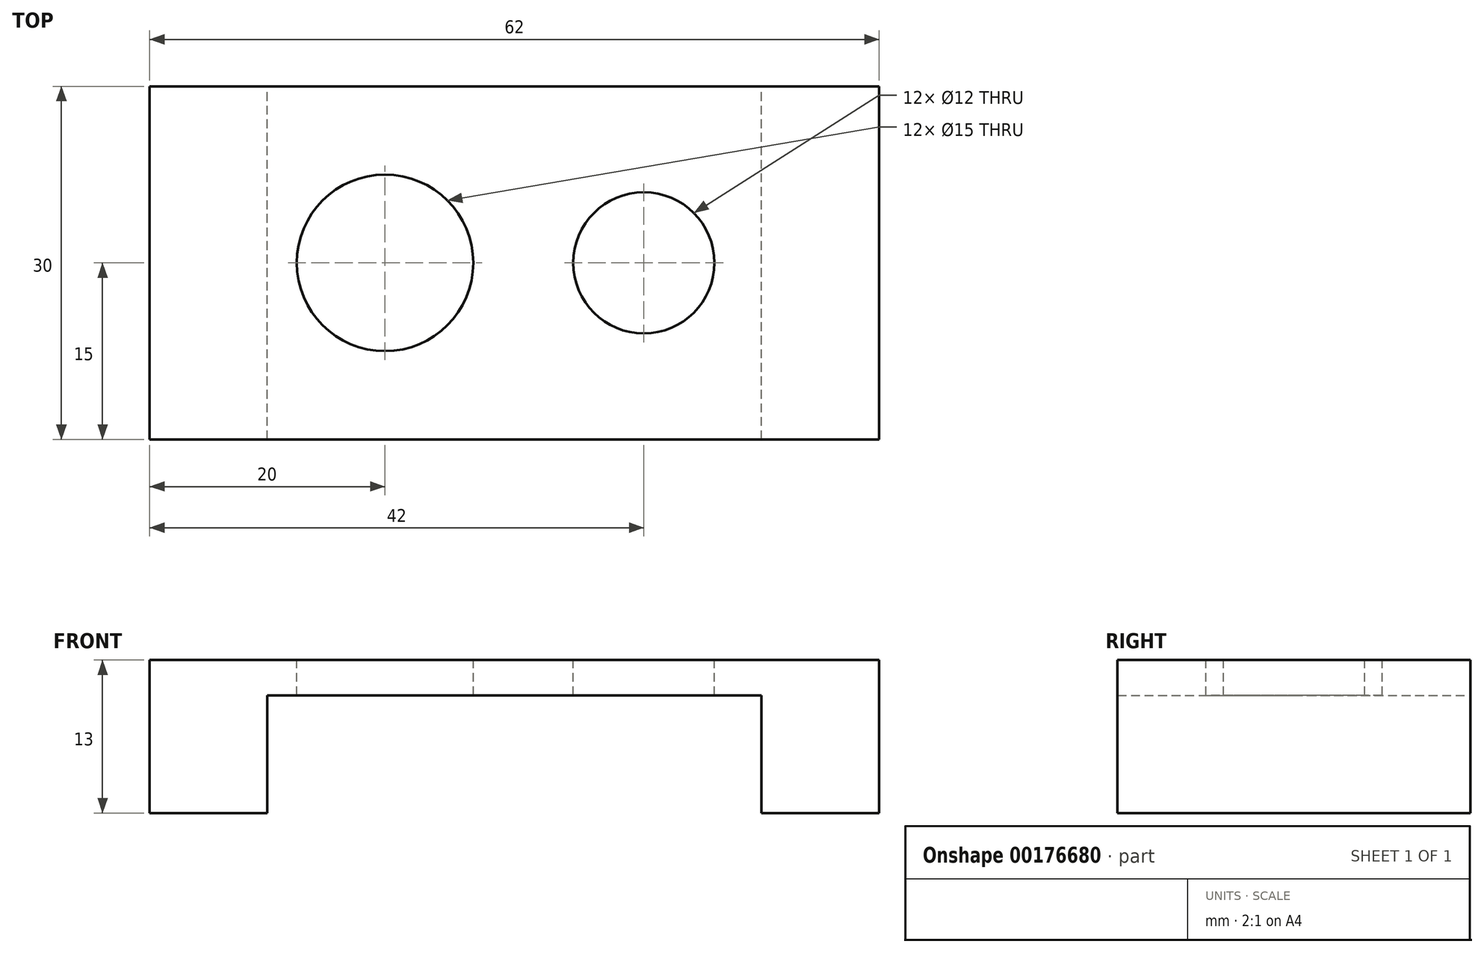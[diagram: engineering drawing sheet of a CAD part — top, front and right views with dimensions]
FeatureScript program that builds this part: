
annotation { "Feature Type Name" : "Feature", "Feature Type Description" : "" }
export const myFeature = defineFeature(function(context is Context, id is Id, definition is map)
    precondition{}
    {
        {
            var Q0;
            Q0=qCreatedBy(makeId("Front.planeOp"),FACE);
            var sketch = newSketch(context, id + "F0", { "sketchPlane" : qUnion([Q0])});
            skLineSegment(sketch, "E0", {"start": v(0, 0) * mm, "end": v(0, -13) * mm});
            skLineSegment(sketch, "E1", {"start": v(0, -13) * mm, "end": v(10, -13) * mm});
            skLineSegment(sketch, "E2", {"start": v(10, -13) * mm, "end": v(10, -3) * mm});
            skLineSegment(sketch, "E3", {"start": v(10, -3) * mm, "end": v(52, -3) * mm});
            skLineSegment(sketch, "E4", {"start": v(52, -3) * mm, "end": v(52, -13) * mm});
            skLineSegment(sketch, "E5", {"start": v(52, -13) * mm, "end": v(62, -13) * mm});
            skLineSegment(sketch, "E6", {"start": v(62, -13) * mm, "end": v(62, 0) * mm});
            skLineSegment(sketch, "E7", {"start": v(0, 0) * mm, "end": v(62, 0) * mm});
            skSolve(sketch);
        }
        {
            var Q0;
            Q0=makeQuery(id+"F0.imprint","IMPRINT",FACE,{"disambiguationData":[TD([[makeQuery(id+"F0.imprint","IMPRINT",EDGE,{"derivedFrom":sQuery(id+"F0.wireOp",EDGE,"E0")}),1.0]])]});
            extrude(context, id + "F1", {"entities" : qUnion([Q0]), "depth" : 30 * mm});
        }
        {
            var Q0;
            Q0=makeQuery(id+"F1.opExtrude","SWEPT_FACE",FACE,{"disambiguationData":[OSD([sQuery(id+"F0.wireOp",EDGE,"E7")])]});
            var sketch = newSketch(context, id + "F2", { "sketchPlane" : qUnion([Q0])});
            skCircle(sketch, "E8", {"center": v(20, -15) * mm, "radius": 7.5 * mm});
            skCircle(sketch, "E9", {"center": v(42, -15) * mm, "radius": 6 * mm});
            skSolve(sketch);
        }
        {
            var Q0;
            Q0=makeQuery(id+"F2.imprint","IMPRINT",FACE,{"disambiguationData":[TD([[makeQuery(id+"F2.imprint","IMPRINT",EDGE,{"derivedFrom":sQuery(id+"F2.wireOp",EDGE,"E8")}),1.0]])]});
            var Q1;
            Q1=makeQuery(id+"F2.imprint","IMPRINT",FACE,{"disambiguationData":[TD([[makeQuery(id+"F2.imprint","IMPRINT",EDGE,{"derivedFrom":sQuery(id+"F2.wireOp",EDGE,"E9")}),1.0]])]});
            extrude(context, id + "F3", {"entities" : qUnion([Q0, Q1]), "operationType" : NewBodyOperationType.REMOVE, "endBound" : BoundingType.THROUGH_ALL, "oppositeDirection" : true, "depth" : 5 * mm});
        }
    });
